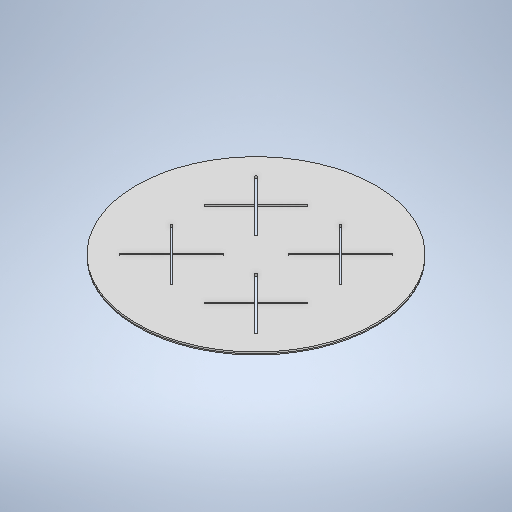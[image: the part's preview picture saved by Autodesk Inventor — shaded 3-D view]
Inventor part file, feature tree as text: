
AUTODESK INVENTOR PART (.ipt)
format: ipt  version: 2025.2 (Build 292293000, 293)  size: 361,984 bytes
history: native  units: mm
features: extrude x3, sketch x3, chamfer x1
ambient origin geometry x8: Origin, YZ Plane, XZ Plane, XY Plane, X Axis, Y Axis, Z Axis, Center Point
bodies: Solid1 (feature_tree)
feature tree (7):
  extrude  "Extrusion1"  Depth=4.7625mm TaperAngle=0.0deg
  chamfer  "Chamfer1"  Distance=2.0mm
  extrude  "Extrusion2"  Depth=2.374mm
  extrude  "Extrusion3"  Depth=10.0mm TaperAngle=0.0deg
  sketch  "Sketch1"  dims[d0=400.0mm d1=4.7625mm d2=0.0mm d3=2.0mm d4=2.0mm d5=2.181662mm]
  sketch  "Sketch2"  dims[d16=2.374mm d20=47.619mm]
  sketch  "Sketch3"  dims[d21=10.0mm d22=0.0mm d28=10.0mm d29=0.0mm]
